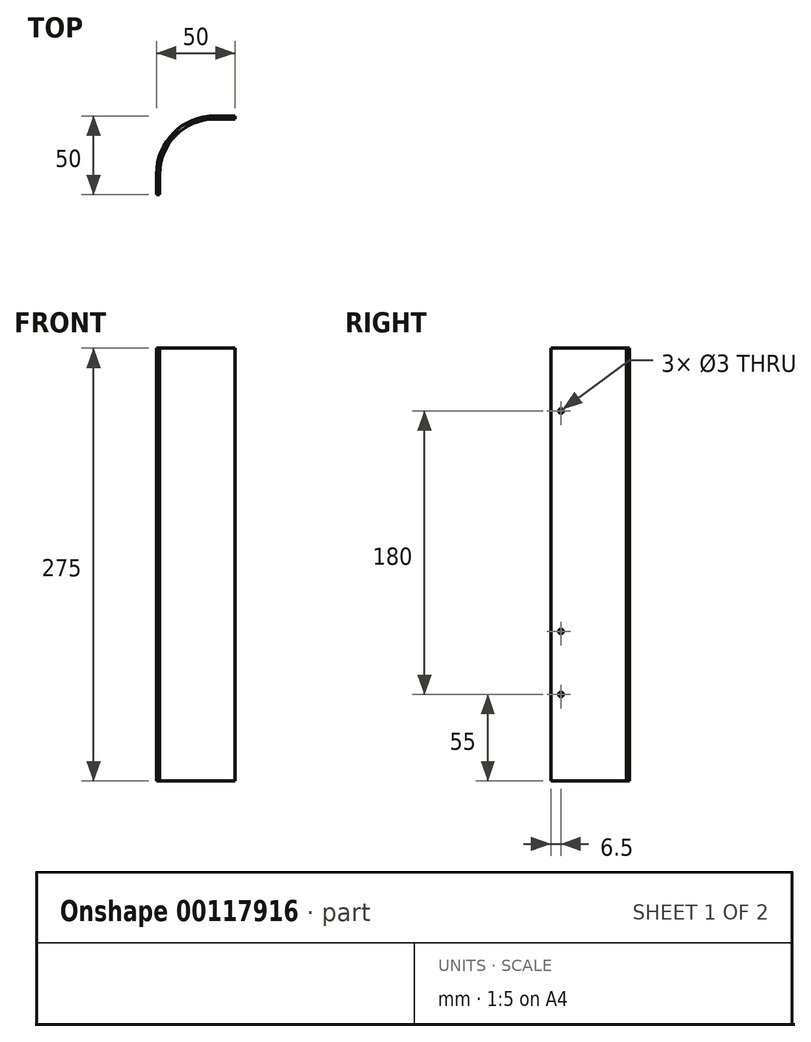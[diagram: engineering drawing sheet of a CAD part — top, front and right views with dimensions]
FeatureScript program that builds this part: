
annotation { "Feature Type Name" : "Feature", "Feature Type Description" : "" }
export const myFeature = defineFeature(function(context is Context, id is Id, definition is map)
    precondition{}
    {
        {
            var Q0;
            Q0=qCreatedBy(makeId("Top.planeOp"),FACE);
            var sketch = newSketch(context, id + "F0", { "sketchPlane" : qUnion([Q0])});
            skLineSegment(sketch, "E0", {"start": v(0, 0) * mm, "end": v(2, 0) * mm});
            skLineSegment(sketch, "E1", {"start": v(2, 0) * mm, "end": v(2, 13) * mm});
            skLineSegment(sketch, "E2", {"start": v(37, 48) * mm, "end": v(50, 48) * mm});
            skLineSegment(sketch, "E3", {"start": v(0, 0) * mm, "end": v(0, 13) * mm});
            skLineSegment(sketch, "E4", {"start": v(37, 50) * mm, "end": v(50, 50) * mm});
            skLineSegment(sketch, "E5", {"start": v(50, 50) * mm, "end": v(50, 48) * mm});
            skPoint(sketch, "E6.visualSharp", {"position": v(2, 48) * mm});
            skArc(sketch, "E6.filletArc", {"start": v(37, 48) * mm, "mid": v(12.25, 37.75) * mm, "end": v(2, 13) * mm});
            skPoint(sketch, "E7.visualSharp", {"position": v(0, 50) * mm});
            skArc(sketch, "E7.filletArc", {"start": v(37, 50) * mm, "mid": v(10.84, 39.16) * mm, "end": v(0, 13) * mm});
            skSolve(sketch);
        }
        {
            var Q0;
            Q0 = qSketchRegion(id + "F0", true);
            extrude(context, id + "F1", {"entities" : qUnion([Q0]), "depth" : 275 * mm});
        }
        {
            var Q0;
            Q0=makeQuery(id+"F1.opExtrude","SWEPT_FACE",FACE,{"disambiguationData":[OSD([sQuery(id+"F0.wireOp",EDGE,"E3")])]});
            var sketch = newSketch(context, id + "F2", { "sketchPlane" : qUnion([Q0])});
            skCircle(sketch, "E8", {"center": v(-6.5, 55) * mm, "radius": 1.5 * mm});
            skCircle(sketch, "E9", {"center": v(-6.5, 95) * mm, "radius": 1.5 * mm});
            skLineSegment(sketch, "E10", {"start": v(-6.5, 0) * mm, "end": v(-6.5, 275) * mm, "construction": true});
            skCircle(sketch, "E11", {"center": v(-6.5, 235) * mm, "radius": 1.5 * mm});
            skSolve(sketch);
        }
        {
            var Q0;
            Q0=makeQuery(id+"F2.imprint","IMPRINT",FACE,{"disambiguationData":[TD([[makeQuery(id+"F2.imprint","IMPRINT",EDGE,{"derivedFrom":sQuery(id+"F2.wireOp",EDGE,"E11")}),1.0]])]});
            var Q1;
            Q1=makeQuery(id+"F2.imprint","IMPRINT",FACE,{"disambiguationData":[TD([[makeQuery(id+"F2.imprint","IMPRINT",EDGE,{"derivedFrom":sQuery(id+"F2.wireOp",EDGE,"E9")}),1.0]])]});
            var Q2;
            Q2=makeQuery(id+"F2.imprint","IMPRINT",FACE,{"disambiguationData":[TD([[makeQuery(id+"F2.imprint","IMPRINT",EDGE,{"derivedFrom":sQuery(id+"F2.wireOp",EDGE,"E8")}),1.0]])]});
            extrude(context, id + "F3", {"entities" : qUnion([Q0, Q1, Q2]), "operationType" : NewBodyOperationType.REMOVE, "endBound" : BoundingType.THROUGH_ALL, "oppositeDirection" : true, "depth" : 25 * mm});
        }
    });
